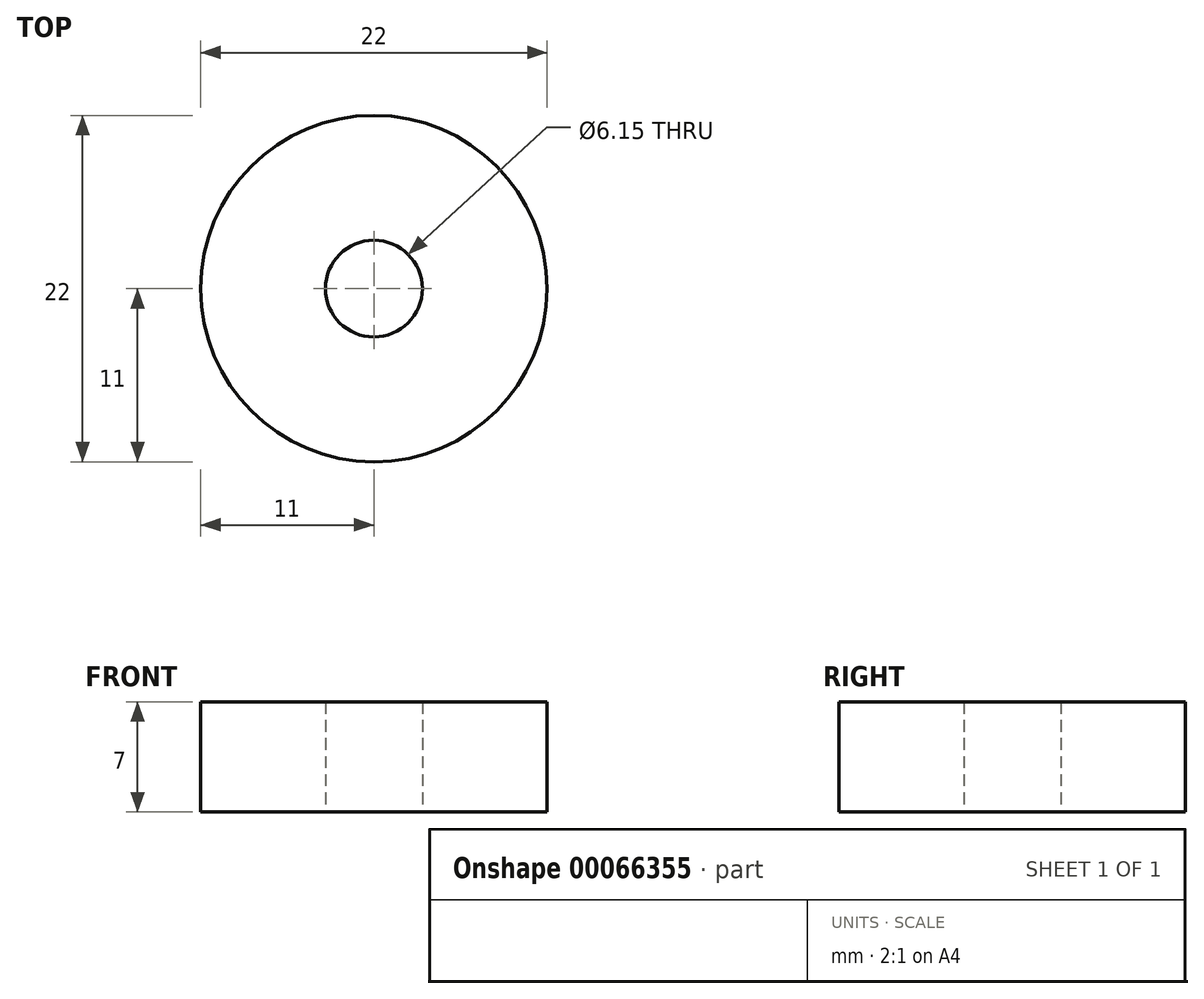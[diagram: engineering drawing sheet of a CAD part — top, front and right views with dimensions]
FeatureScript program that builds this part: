
annotation { "Feature Type Name" : "Feature", "Feature Type Description" : "" }
export const myFeature = defineFeature(function(context is Context, id is Id, definition is map)
    precondition{}
    {
        {
            var Q0;
            Q0=qCreatedBy(makeId("Top.planeOp"),FACE);
            var sketch = newSketch(context, id + "F0", { "sketchPlane" : qUnion([Q0])});
            skCircle(sketch, "E0", {"center": v(0, 0) * mm, "radius": 11 * mm});
            skCircle(sketch, "E1", {"center": v(0, 0) * mm, "radius": 3.08 * mm});
            skSolve(sketch);
        }
        {
            var Q0;
            Q0=makeQuery(id+"F0.imprint","IMPRINT",FACE,{"disambiguationData":[TD([[makeQuery(id+"F0.imprint","IMPRINT",EDGE,{"derivedFrom":sQuery(id+"F0.wireOp",EDGE,"E0")}),1.0]])]});
            extrude(context, id + "F1", {"entities" : qUnion([Q0]), "depth" : 7 * mm});
        }
    });
